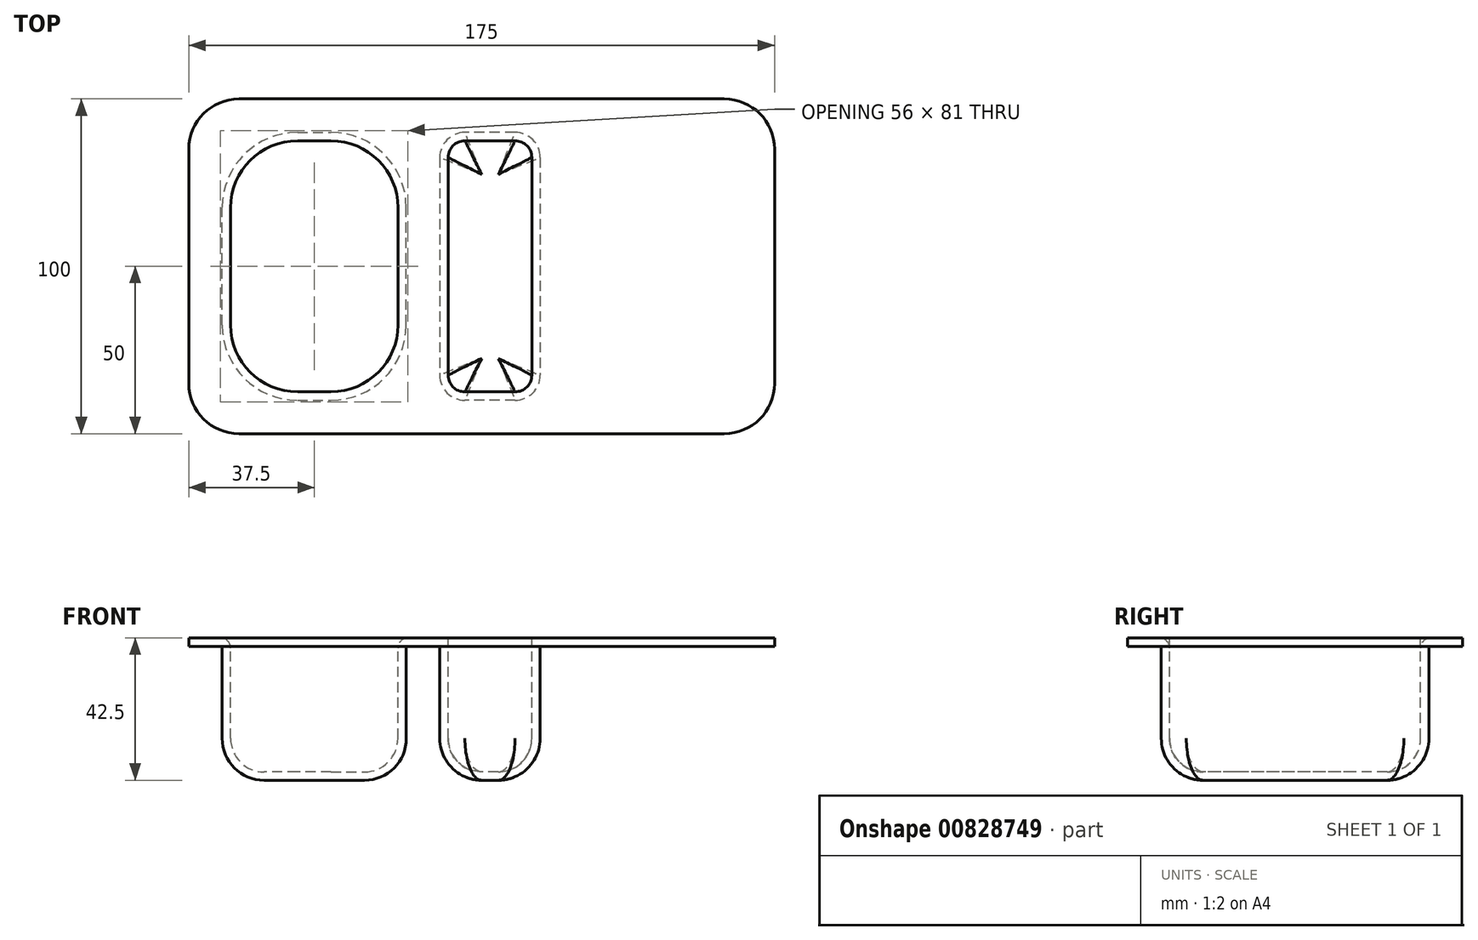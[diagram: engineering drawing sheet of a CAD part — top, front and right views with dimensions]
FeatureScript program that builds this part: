
annotation { "Feature Type Name" : "Feature", "Feature Type Description" : "" }
export const myFeature = defineFeature(function(context is Context, id is Id, definition is map)
    precondition{}
    {
        {
            var Q0;
            Q0=qCreatedBy(makeId("Top.planeOp"),FACE);
            var sketch = newSketch(context, id + "F0", { "sketchPlane" : qUnion([Q0])});
            skLineSegment(sketch, "E0.bottom", {"start": v(72.5, -50) * mm, "end": v(-72.5, -50) * mm});
            skLineSegment(sketch, "E0.top", {"start": v(72.5, 50) * mm, "end": v(-72.5, 50) * mm});
            skLineSegment(sketch, "E0.left", {"start": v(87.5, -35) * mm, "end": v(87.5, 35) * mm});
            skLineSegment(sketch, "E0.right", {"start": v(-87.5, -35) * mm, "end": v(-87.5, 35) * mm});
            skPoint(sketch, "E0.middle", {"position": v(0, 0) * mm});
            skPoint(sketch, "E1.visualSharp", {"position": v(-87.5, -50) * mm});
            skArc(sketch, "E1.filletArc", {"start": v(-87.5, -35) * mm, "mid": v(-83.1, -45.6) * mm, "end": v(-72.5, -50) * mm});
            skPoint(sketch, "E2.visualSharp", {"position": v(-87.5, 50) * mm});
            skArc(sketch, "E2.filletArc", {"start": v(-72.5, 50) * mm, "mid": v(-83.1, 45.6) * mm, "end": v(-87.5, 35) * mm});
            skPoint(sketch, "E3.visualSharp", {"position": v(87.5, 50) * mm});
            skArc(sketch, "E3.filletArc", {"start": v(87.5, 35) * mm, "mid": v(83.1, 45.6) * mm, "end": v(72.5, 50) * mm});
            skPoint(sketch, "E4.visualSharp", {"position": v(87.5, -50) * mm});
            skArc(sketch, "E4.filletArc", {"start": v(72.5, -50) * mm, "mid": v(83.1, -45.6) * mm, "end": v(87.5, -35) * mm});
            skSolve(sketch);
        }
        {
            var Q0;
            Q0=makeQuery(id+"F0.imprint","IMPRINT",FACE,{"disambiguationData":[TD([[makeQuery(id+"F0.imprint","IMPRINT",EDGE,{"derivedFrom":sQuery(id+"F0.wireOp",EDGE,"E0.bottom")}),-1.0]])]});
            extrude(context, id + "F1", {"entities" : qUnion([Q0]), "depth" : 50 * mm, "offsetDistance" : 25 * mm});
        }
        {
            var Q0;
            Q0=makeQuery(id+"F1.opExtrude","CAP_FACE",FACE,{"disambiguationData":[OSD([sQuery(id+"F0.wireOp",EDGE,"E0.bottom"),sQuery(id+"F0.wireOp",EDGE,"E0.top"),sQuery(id+"F0.wireOp",EDGE,"E0.left"),sQuery(id+"F0.wireOp",EDGE,"E0.right"),sQuery(id+"F0.wireOp",EDGE,"E1.filletArc"),sQuery(id+"F0.wireOp",EDGE,"E2.filletArc"),sQuery(id+"F0.wireOp",EDGE,"E3.filletArc"),sQuery(id+"F0.wireOp",EDGE,"E4.filletArc")])],"isStart":false});
            var sketch = newSketch(context, id + "F2", { "sketchPlane" : qUnion([Q0])});
            skLineSegment(sketch, "E5", {"start": v(87.5, 0) * mm, "end": v(-79.55, 0) * mm, "construction": true});
            skLineSegment(sketch, "E6.bottom", {"start": v(-25, 37.5) * mm, "end": v(-75, 37.5) * mm});
            skLineSegment(sketch, "E6.top", {"start": v(-25, -37.5) * mm, "end": v(-75, -37.5) * mm});
            skLineSegment(sketch, "E6.left", {"start": v(-25, 37.5) * mm, "end": v(-25, -37.5) * mm});
            skLineSegment(sketch, "E6.right", {"start": v(-75, 37.5) * mm, "end": v(-75, -37.5) * mm});
            skPoint(sketch, "E6.middle", {"position": v(-50, 0) * mm});
            skLineSegment(sketch, "E7.bottom", {"start": v(15, 37.5) * mm, "end": v(-10, 37.5) * mm});
            skLineSegment(sketch, "E7.top", {"start": v(15, -37.5) * mm, "end": v(-10, -37.5) * mm});
            skLineSegment(sketch, "E7.left", {"start": v(15, 37.5) * mm, "end": v(15, -37.5) * mm});
            skLineSegment(sketch, "E7.right", {"start": v(-10, 37.5) * mm, "end": v(-10, -37.5) * mm});
            skPoint(sketch, "E7.middle", {"position": v(2.5, 0) * mm});
            skLineSegment(sketch, "E8.bottom", {"start": v(25.27, 4) * mm, "end": v(75.27, 4) * mm});
            skLineSegment(sketch, "E8.top", {"start": v(25.27, -4) * mm, "end": v(75.27, -4) * mm});
            skLineSegment(sketch, "E8.left", {"start": v(25.27, 4) * mm, "end": v(25.27, -4) * mm});
            skLineSegment(sketch, "E8.right", {"start": v(75.27, 4) * mm, "end": v(75.27, -4) * mm});
            skPoint(sketch, "E8.middle", {"position": v(50.27, 0) * mm});
            skSolve(sketch);
        }
        {
            var Q0;
            Q0=makeQuery(id+"F2.imprint","IMPRINT",FACE,{"disambiguationData":[TD([[makeQuery(id+"F2.imprint","IMPRINT",EDGE,{"derivedFrom":sQuery(id+"F2.wireOp",EDGE,"E6.bottom")}),1.0]])]});
            var Q1;
            Q1=makeQuery(id+"F2.imprint","IMPRINT",FACE,{"disambiguationData":[TD([[makeQuery(id+"F2.imprint","IMPRINT",EDGE,{"derivedFrom":sQuery(id+"F2.wireOp",EDGE,"E7.bottom")}),1.0]])]});
            extrude(context, id + "F3", {"entities" : qUnion([Q0, Q1]), "operationType" : NewBodyOperationType.REMOVE, "oppositeDirection" : true, "depth" : 40 * mm, "offsetDistance" : 25 * mm});
        }
        {
            var Q0;
            Q0=makeQuery(id+"F3.boolean.opBoolean","COPY",FACE,{"derivedFrom":makeQuery(id+"F3.opExtrude","CAP_FACE",FACE,{"disambiguationData":[OSD([sQuery(id+"F2.wireOp",EDGE,"E6.bottom"),sQuery(id+"F2.wireOp",EDGE,"E6.top"),sQuery(id+"F2.wireOp",EDGE,"E6.left"),sQuery(id+"F2.wireOp",EDGE,"E6.right")])],"isStart":false})});
            var Q1;
            Q1=makeQuery(id+"F3.boolean.opBoolean","COPY",FACE,{"derivedFrom":makeQuery(id+"F3.opExtrude","CAP_FACE",FACE,{"disambiguationData":[OSD([sQuery(id+"F2.wireOp",EDGE,"E7.bottom"),sQuery(id+"F2.wireOp",EDGE,"E7.top"),sQuery(id+"F2.wireOp",EDGE,"E7.left"),sQuery(id+"F2.wireOp",EDGE,"E7.right")])],"isStart":false})});
            fillet(context, id + "F4", {"entities" : qUnion([Q0, Q1]), "radius" : 10 * mm, "tangentPropagation" : true, "allowEdgeOverflow" : false});
        }
        {
            var Q0;
            Q0=makeQuery(id+"F3.boolean.opBoolean","COPY",EDGE,{"derivedFrom":makeQuery(id+"F3.opExtrude","SWEPT_EDGE",EDGE,{"disambiguationData":[OSD([sQuery(id+"F2.wireOp",EDGE,"E6.bottom"),sQuery(id+"F2.wireOp",EDGE,"E6.right")])]})});
            var Q1;
            Q1=makeQuery(id+"F3.boolean.opBoolean","COPY",EDGE,{"derivedFrom":makeQuery(id+"F3.opExtrude","SWEPT_EDGE",EDGE,{"disambiguationData":[OSD([sQuery(id+"F2.wireOp",EDGE,"E6.bottom"),sQuery(id+"F2.wireOp",EDGE,"E6.left")])]})});
            var Q2;
            Q2=makeQuery(id+"F3.boolean.opBoolean","COPY",EDGE,{"derivedFrom":makeQuery(id+"F3.opExtrude","SWEPT_EDGE",EDGE,{"disambiguationData":[OSD([sQuery(id+"F2.wireOp",EDGE,"E6.top"),sQuery(id+"F2.wireOp",EDGE,"E6.right")])]})});
            var Q3;
            Q3=makeQuery(id+"F3.boolean.opBoolean","COPY",EDGE,{"derivedFrom":makeQuery(id+"F3.opExtrude","SWEPT_EDGE",EDGE,{"disambiguationData":[OSD([sQuery(id+"F2.wireOp",EDGE,"E6.top"),sQuery(id+"F2.wireOp",EDGE,"E6.left")])]})});
            fillet(context, id + "F5", {"entities" : qUnion([Q0, Q1, Q2, Q3]), "radius" : 20 * mm, "tangentPropagation" : true, "allowEdgeOverflow" : false});
        }
        {
            var Q0;
            Q0=makeQuery(id+"F3.boolean.opBoolean","COPY",EDGE,{"derivedFrom":makeQuery(id+"F3.opExtrude","SWEPT_EDGE",EDGE,{"disambiguationData":[OSD([sQuery(id+"F2.wireOp",EDGE,"E7.bottom"),sQuery(id+"F2.wireOp",EDGE,"E7.right")])]})});
            var Q1;
            Q1=makeQuery(id+"F3.boolean.opBoolean","COPY",EDGE,{"derivedFrom":makeQuery(id+"F3.opExtrude","SWEPT_EDGE",EDGE,{"disambiguationData":[OSD([sQuery(id+"F2.wireOp",EDGE,"E7.bottom"),sQuery(id+"F2.wireOp",EDGE,"E7.left")])]})});
            var Q2;
            Q2=makeQuery(id+"F3.boolean.opBoolean","COPY",EDGE,{"derivedFrom":makeQuery(id+"F3.opExtrude","SWEPT_EDGE",EDGE,{"disambiguationData":[OSD([sQuery(id+"F2.wireOp",EDGE,"E7.top"),sQuery(id+"F2.wireOp",EDGE,"E7.right")])]})});
            var Q3;
            Q3=makeQuery(id+"F3.boolean.opBoolean","COPY",EDGE,{"derivedFrom":makeQuery(id+"F3.opExtrude","SWEPT_EDGE",EDGE,{"disambiguationData":[OSD([sQuery(id+"F2.wireOp",EDGE,"E7.top"),sQuery(id+"F2.wireOp",EDGE,"E7.left")])]})});
            fillet(context, id + "F6", {"entities" : qUnion([Q0, Q1, Q2, Q3]), "radius" : 5 * mm, "tangentPropagation" : true, "allowEdgeOverflow" : false});
        }
        {
            var Q0;
            Q0=makeQuery(id+"F5.opFillet","BLEND_EDGE",EDGE,{"blendedFrom":[makeQuery(id+"F3.boolean.opBoolean","COPY",EDGE,{"derivedFrom":makeQuery(id+"F3.opExtrude","SWEPT_EDGE",EDGE,{"disambiguationData":[OSD([sQuery(id+"F2.wireOp",EDGE,"E6.bottom"),sQuery(id+"F2.wireOp",EDGE,"E6.right")])]})}),makeQuery(id+"F1.opExtrude","CAP_FACE",FACE,{"disambiguationData":[OSD([sQuery(id+"F0.wireOp",EDGE,"E0.bottom"),sQuery(id+"F0.wireOp",EDGE,"E0.top"),sQuery(id+"F0.wireOp",EDGE,"E0.left"),sQuery(id+"F0.wireOp",EDGE,"E0.right"),sQuery(id+"F0.wireOp",EDGE,"E1.filletArc"),sQuery(id+"F0.wireOp",EDGE,"E2.filletArc"),sQuery(id+"F0.wireOp",EDGE,"E3.filletArc"),sQuery(id+"F0.wireOp",EDGE,"E4.filletArc")])],"isStart":false})],"blendedInto":[makeQuery(id+"F1.opExtrude","CAP_FACE",FACE,{"disambiguationData":[OSD([sQuery(id+"F0.wireOp",EDGE,"E0.bottom"),sQuery(id+"F0.wireOp",EDGE,"E0.top"),sQuery(id+"F0.wireOp",EDGE,"E0.left"),sQuery(id+"F0.wireOp",EDGE,"E0.right"),sQuery(id+"F0.wireOp",EDGE,"E1.filletArc"),sQuery(id+"F0.wireOp",EDGE,"E2.filletArc"),sQuery(id+"F0.wireOp",EDGE,"E3.filletArc"),sQuery(id+"F0.wireOp",EDGE,"E4.filletArc")])],"isStart":false})]});
            var Q1;
            Q1=makeQuery(id+"F3.boolean.opBoolean","COPY",EDGE,{"derivedFrom":makeQuery(id+"F3.opExtrude","CAP_EDGE",EDGE,{"disambiguationData":[OSD([sQuery(id+"F2.wireOp",EDGE,"E7.right")])],"isStart":true})});
            fillet(context, id + "F7", {"entities" : qUnion([Q0, Q1]), "radius" : 3 * mm, "tangentPropagation" : true, "allowEdgeOverflow" : false});
        }
        {
            var Q0;
            Q0=makeQuery(id+"F1.opExtrude","SWEPT_FACE",FACE,{"disambiguationData":[OSD([sQuery(id+"F0.wireOp",EDGE,"E0.bottom")])]});
            var Q1;
            Q1=makeQuery(id+"F1.opExtrude","SWEPT_FACE",FACE,{"disambiguationData":[OSD([sQuery(id+"F0.wireOp",EDGE,"E1.filletArc")])]});
            var Q2;
            Q2=makeQuery(id+"F1.opExtrude","SWEPT_FACE",FACE,{"disambiguationData":[OSD([sQuery(id+"F0.wireOp",EDGE,"E0.right")])]});
            var Q3;
            Q3=makeQuery(id+"F1.opExtrude","SWEPT_FACE",FACE,{"disambiguationData":[OSD([sQuery(id+"F0.wireOp",EDGE,"E4.filletArc")])]});
            var Q4;
            Q4=makeQuery(id+"F1.opExtrude","SWEPT_FACE",FACE,{"disambiguationData":[OSD([sQuery(id+"F0.wireOp",EDGE,"E0.left")])]});
            var Q5;
            Q5=makeQuery(id+"F1.opExtrude","SWEPT_FACE",FACE,{"disambiguationData":[OSD([sQuery(id+"F0.wireOp",EDGE,"E3.filletArc")])]});
            var Q6;
            Q6=makeQuery(id+"F1.opExtrude","SWEPT_FACE",FACE,{"disambiguationData":[OSD([sQuery(id+"F0.wireOp",EDGE,"E0.top")])]});
            var Q7;
            Q7=makeQuery(id+"F1.opExtrude","SWEPT_FACE",FACE,{"disambiguationData":[OSD([sQuery(id+"F0.wireOp",EDGE,"E2.filletArc")])]});
            var Q8;
            Q8=makeQuery(id+"F1.opExtrude","CAP_FACE",FACE,{"disambiguationData":[OSD([sQuery(id+"F0.wireOp",EDGE,"E0.bottom"),sQuery(id+"F0.wireOp",EDGE,"E0.top"),sQuery(id+"F0.wireOp",EDGE,"E0.left"),sQuery(id+"F0.wireOp",EDGE,"E0.right"),sQuery(id+"F0.wireOp",EDGE,"E1.filletArc"),sQuery(id+"F0.wireOp",EDGE,"E2.filletArc"),sQuery(id+"F0.wireOp",EDGE,"E3.filletArc"),sQuery(id+"F0.wireOp",EDGE,"E4.filletArc")])],"isStart":true});
            shell(context, id + "F8", {"entities" : qUnion([Q0, Q1, Q2, Q3, Q4, Q5, Q6, Q7, Q8]), "thickness" : 2.5 * mm});
        }
    });
